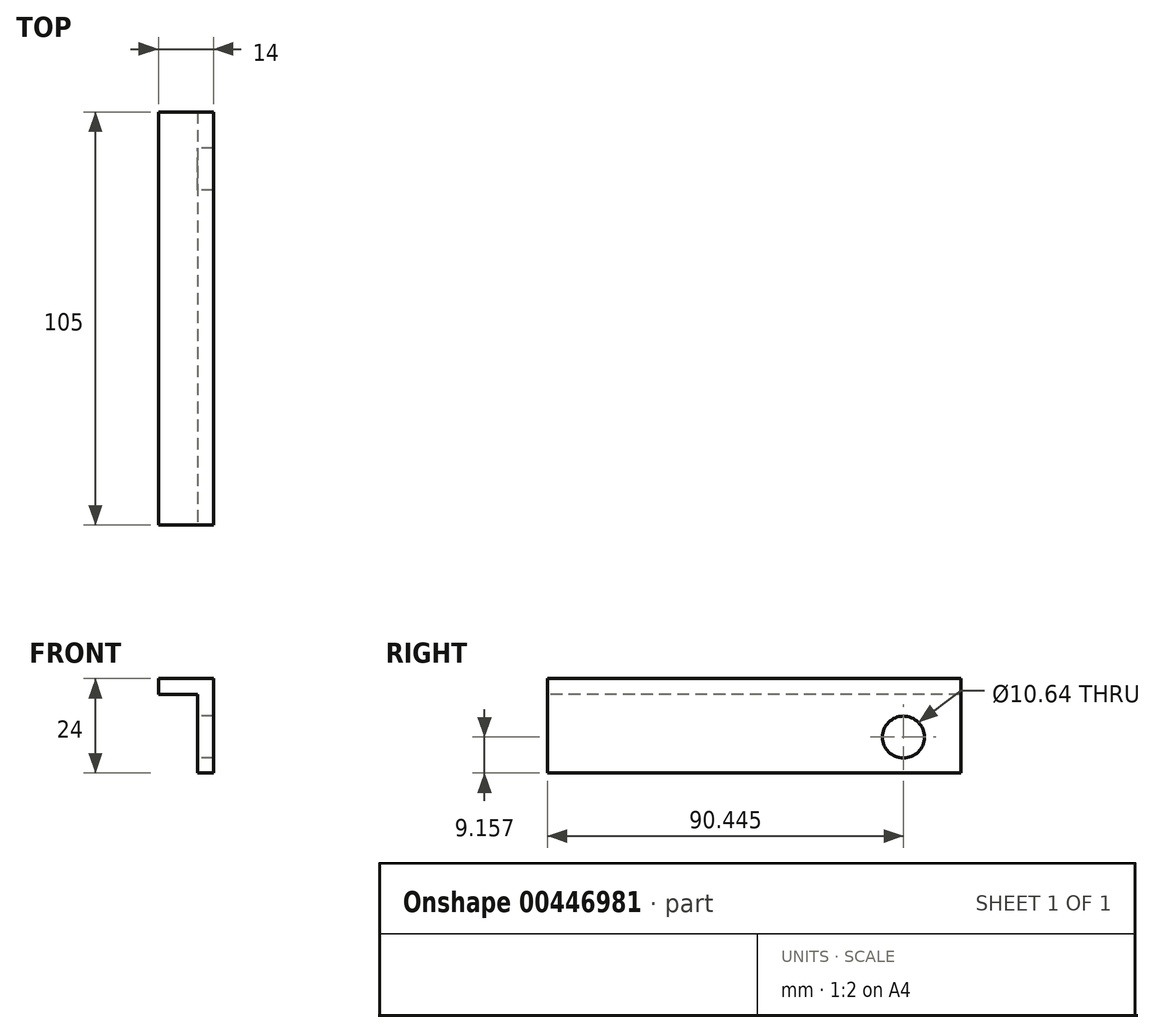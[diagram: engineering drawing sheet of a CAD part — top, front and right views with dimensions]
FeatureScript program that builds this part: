
annotation { "Feature Type Name" : "Feature", "Feature Type Description" : "" }
export const myFeature = defineFeature(function(context is Context, id is Id, definition is map)
    precondition{}
    {
        {
            var Q0;
            Q0=qCreatedBy(makeId("Right.planeOp"),FACE);
            var sketch = newSketch(context, id + "F0", { "sketchPlane" : qUnion([Q0])});
            skLineSegment(sketch, "E0.bottom", {"start": v(52.5, 12) * mm, "end": v(-52.5, 12) * mm});
            skLineSegment(sketch, "E0.top", {"start": v(52.5, -12) * mm, "end": v(-52.5, -12) * mm});
            skLineSegment(sketch, "E0.left", {"start": v(52.5, 12) * mm, "end": v(52.5, -12) * mm});
            skLineSegment(sketch, "E0.right", {"start": v(-52.5, 12) * mm, "end": v(-52.5, -12) * mm});
            skPoint(sketch, "E0.middle", {"position": v(0, 0) * mm});
            skSolve(sketch);
        }
        {
            var Q0;
            Q0 = qSketchRegion(id + "F0", true);
            extrude(context, id + "F1", {"entities" : qUnion([Q0]), "depth" : 2 * mm, "hasSecondDirection" : true, "secondDirectionOppositeDirection" : true, "secondDirectionDepth" : 2 * mm});
        }
        {
            var Q0;
            Q0=makeQuery(id+"F1.opExtrude","CAP_FACE",FACE,{"disambiguationData":[OSD([sQuery(id+"F0.wireOp",EDGE,"E0.bottom"),sQuery(id+"F0.wireOp",EDGE,"E0.top"),sQuery(id+"F0.wireOp",EDGE,"E0.left"),sQuery(id+"F0.wireOp",EDGE,"E0.right")])],"isStart":true});
            var sketch = newSketch(context, id + "F2", { "sketchPlane" : qUnion([Q0])});
            skLineSegment(sketch, "E1.bottom", {"start": v(-52.5, 12) * mm, "end": v(52.5, 12) * mm});
            skLineSegment(sketch, "E1.top", {"start": v(-52.5, 8) * mm, "end": v(52.5, 8) * mm});
            skLineSegment(sketch, "E1.left", {"start": v(-52.5, 12) * mm, "end": v(-52.5, 8) * mm});
            skLineSegment(sketch, "E1.right", {"start": v(52.5, 12) * mm, "end": v(52.5, 8) * mm});
            skSolve(sketch);
        }
        {
            var Q0;
            Q0 = qSketchRegion(id + "F2", true);
            extrude(context, id + "F3", {"entities" : qUnion([Q0]), "operationType" : NewBodyOperationType.ADD, "depth" : 10 * mm});
        }
        {
            var Q0;
            Q0=makeQuery(id+"F1.opExtrude","CAP_FACE",FACE,{"disambiguationData":[OSD([sQuery(id+"F0.wireOp",EDGE,"E0.bottom"),sQuery(id+"F0.wireOp",EDGE,"E0.top"),sQuery(id+"F0.wireOp",EDGE,"E0.left"),sQuery(id+"F0.wireOp",EDGE,"E0.right")])],"isStart":true});
            var sketch = newSketch(context, id + "F4", { "sketchPlane" : qUnion([Q0])});
            skCircle(sketch, "E2", {"center": v(-37.95, -2.84) * mm, "radius": 5.32 * mm});
            skSolve(sketch);
        }
        {
            var Q0;
            Q0 = qSketchRegion(id + "F4", true);
            extrude(context, id + "F5", {"entities" : qUnion([Q0]), "operationType" : NewBodyOperationType.REMOVE, "endBound" : BoundingType.THROUGH_ALL, "oppositeDirection" : true, "depth" : 25 * mm});
        }
    });
